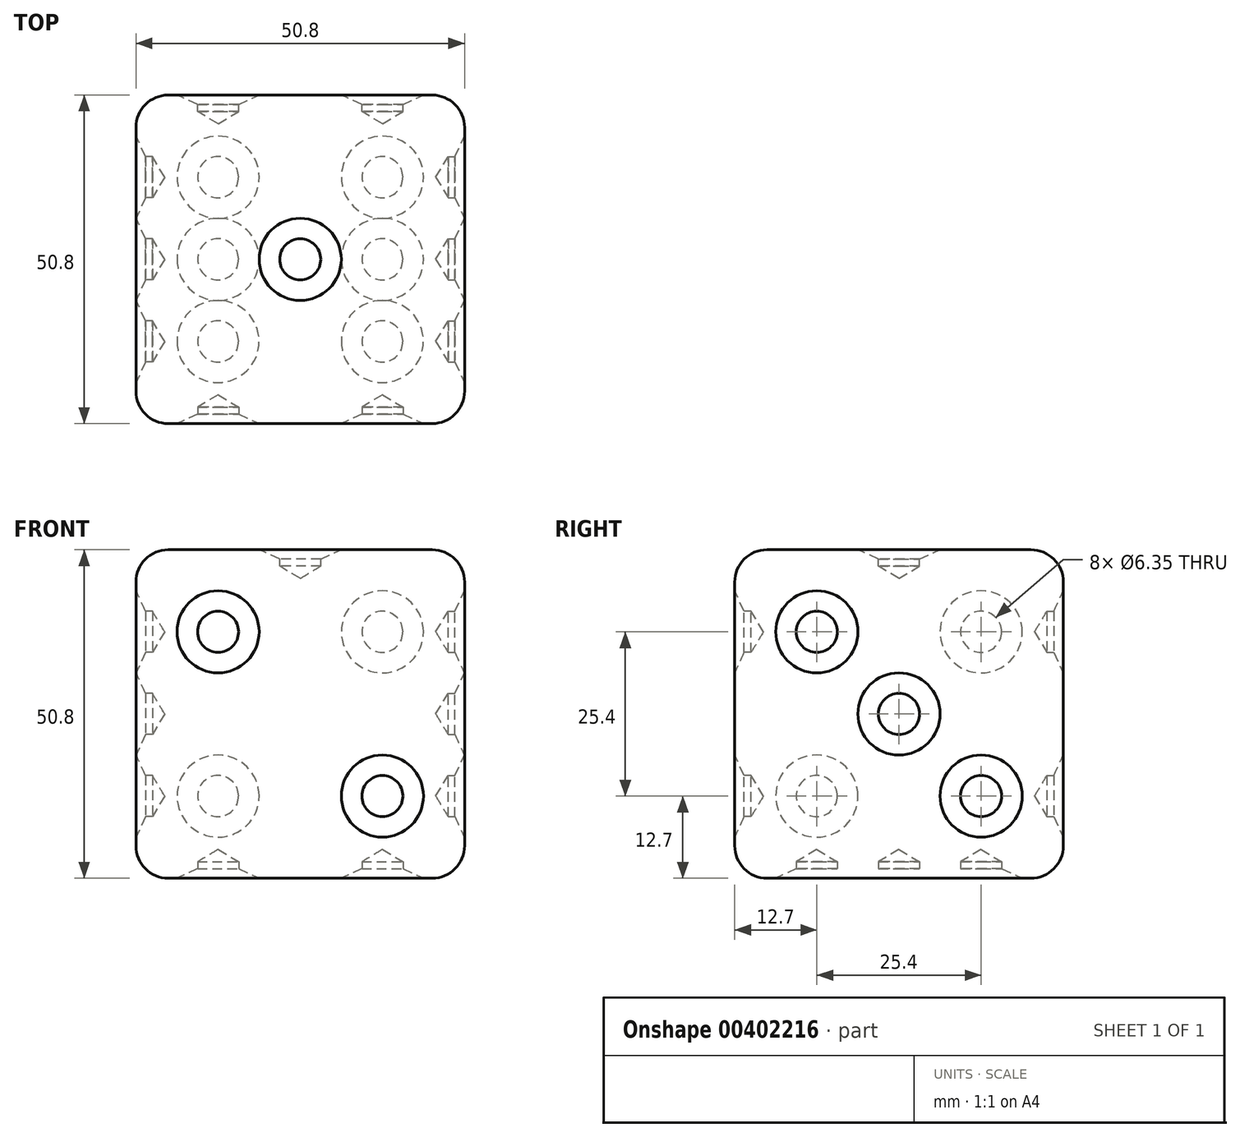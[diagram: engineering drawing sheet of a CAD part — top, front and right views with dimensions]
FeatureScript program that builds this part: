
annotation { "Feature Type Name" : "Feature", "Feature Type Description" : "" }
export const myFeature = defineFeature(function(context is Context, id is Id, definition is map)
    precondition{}
    {
        {
            var Q0;
            Q0=qCreatedBy(makeId("Top.planeOp"),FACE);
            var sketch = newSketch(context, id + "F0", { "sketchPlane" : qUnion([Q0])});
            skLineSegment(sketch, "E0.bottom", {"start": v(25.4, 25.4) * mm, "end": v(-25.4, 25.4) * mm});
            skLineSegment(sketch, "E0.top", {"start": v(25.4, -25.4) * mm, "end": v(-25.4, -25.4) * mm});
            skLineSegment(sketch, "E0.left", {"start": v(25.4, 25.4) * mm, "end": v(25.4, -25.4) * mm});
            skLineSegment(sketch, "E0.right", {"start": v(-25.4, 25.4) * mm, "end": v(-25.4, -25.4) * mm});
            skPoint(sketch, "E0.middle", {"position": v(0, 0) * mm});
            skSolve(sketch);
        }
        {
            var Q0;
            Q0=qSketchRegion(id+"F0",true);
            extrude(context, id + "F1", {"entities" : qUnion([Q0]), "depth" : 50.8 * mm});
        }
        {
            var Q0;
            Q0=makeQuery(id+"F1.opExtrude","CAP_FACE",FACE,{"disambiguationData":[OSD([sQuery(id+"F0.wireOp",EDGE,"E0.bottom"),sQuery(id+"F0.wireOp",EDGE,"E0.top"),sQuery(id+"F0.wireOp",EDGE,"E0.left"),sQuery(id+"F0.wireOp",EDGE,"E0.right")])],"isStart":false});
            var sketch = newSketch(context, id + "F2", { "sketchPlane" : qUnion([Q0])});
            skCircle(sketch, "E1", {"center": v(0, 0) * mm, "radius": 4.13 * mm});
            skSolve(sketch);
        }
        {
            var Q0;
            Q0=sQuery(id+"F2.wireOp",VERTEX,"E1.center");
            var Q1;
            Q1=makeQuery(id+"F1.opExtrude","SWEPT_BODY",BODY,{"disambiguationData":[OSD([sQuery(id+"F0.wireOp",EDGE,"E0.bottom"),sQuery(id+"F0.wireOp",EDGE,"E0.top"),sQuery(id+"F0.wireOp",EDGE,"E0.left"),sQuery(id+"F0.wireOp",EDGE,"E0.right")])]});
            hole(context, id + "F3", {"style" : HoleStyle.C_SINK, "endStyle" : HoleEndStyle.BLIND, "holeDiameter" : 6.35 * mm, "cSinkDiameter" : 12.7 * mm, "cSinkAngle" : 130 * degree, "holeDepth" : 2.54 * mm, "isTappedThrough" : true, "tappedDepth" : 12.7 * mm, "tapClearance" : 3, "locations" : qUnion([Q0]), "scope" : qUnion([Q1])});
        }
        {
            var Q0;
            Q0=makeQuery(id+"F1.opExtrude","SWEPT_FACE",FACE,{"disambiguationData":[OSD([sQuery(id+"F0.wireOp",EDGE,"E0.top")])]});
            var sketch = newSketch(context, id + "F4", { "sketchPlane" : qUnion([Q0])});
            skLineSegment(sketch, "E2", {"start": v(-25.4, 50.8) * mm, "end": v(-25.4, 38.1) * mm});
            skLineSegment(sketch, "E3", {"start": v(-12.7, 38.1) * mm, "end": v(-25.4, 38.1) * mm});
            skLineSegment(sketch, "E4", {"start": v(-12.7, 38.1) * mm, "end": v(-12.7, 50.8) * mm});
            skLineSegment(sketch, "E5", {"start": v(-25.4, 50.8) * mm, "end": v(-12.7, 50.8) * mm});
            skLineSegment(sketch, "E6", {"start": v(25.4, 0) * mm, "end": v(12.7, 0) * mm});
            skLineSegment(sketch, "E7", {"start": v(12.7, 0) * mm, "end": v(12.7, 12.7) * mm});
            skLineSegment(sketch, "E8", {"start": v(12.7, 12.7) * mm, "end": v(25.4, 12.7) * mm});
            skLineSegment(sketch, "E9", {"start": v(25.4, 12.7) * mm, "end": v(25.4, 0) * mm});
            skSolve(sketch);
        }
        {
            var Q0;
            Q0=sQuery(id+"F4.wireOp",VERTEX,"E4.start");
            var Q1;
            Q1=sQuery(id+"F4.wireOp",VERTEX,"E8.start");
            var Q2;
            Q2=makeQuery(id+"F1.opExtrude","SWEPT_BODY",BODY,{"disambiguationData":[OSD([sQuery(id+"F0.wireOp",EDGE,"E0.bottom"),sQuery(id+"F0.wireOp",EDGE,"E0.top"),sQuery(id+"F0.wireOp",EDGE,"E0.left"),sQuery(id+"F0.wireOp",EDGE,"E0.right")])]});
            hole(context, id + "F5", {"style" : HoleStyle.C_SINK, "endStyle" : HoleEndStyle.BLIND, "holeDiameter" : 6.35 * mm, "cSinkDiameter" : 12.7 * mm, "cSinkAngle" : 130 * degree, "holeDepth" : 2.54 * mm, "isTappedThrough" : true, "tappedDepth" : 12.7 * mm, "tapClearance" : 3, "locations" : qUnion([Q0, Q1]), "scope" : qUnion([Q2])});
        }
        {
            var Q0;
            Q0=makeQuery(id+"F1.opExtrude","SWEPT_FACE",FACE,{"disambiguationData":[OSD([sQuery(id+"F0.wireOp",EDGE,"E0.left")])]});
            var sketch = newSketch(context, id + "F6", { "sketchPlane" : qUnion([Q0])});
            skLineSegment(sketch, "E10", {"start": v(0, 50.8) * mm, "end": v(0, 0) * mm, "construction": true});
            skLineSegment(sketch, "E11", {"start": v(0, 0) * mm, "end": v(0, 25.4) * mm, "construction": true});
            skLineSegment(sketch, "E12", {"start": v(25.4, 25.4) * mm, "end": v(0, 25.4) * mm, "construction": true});
            skLineSegment(sketch, "E13", {"start": v(0, 25.4) * mm, "end": v(-25.4, 25.4) * mm, "construction": true});
            skCircle(sketch, "E14", {"center": v(0, 25.4) * mm, "radius": 2.62 * mm});
            skLineSegment(sketch, "E15", {"start": v(-12.7, 50.8) * mm, "end": v(-12.7, 38.1) * mm});
            skLineSegment(sketch, "E16", {"start": v(-25.4, 38.1) * mm, "end": v(-25.4, 50.8) * mm});
            skLineSegment(sketch, "E17", {"start": v(-12.7, 50.8) * mm, "end": v(-25.4, 50.8) * mm});
            skLineSegment(sketch, "E18", {"start": v(-12.7, 38.1) * mm, "end": v(-25.4, 38.1) * mm});
            skLineSegment(sketch, "E19", {"start": v(25.4, 50.8) * mm, "end": v(-25.4, 0) * mm, "construction": true});
            skLineSegment(sketch, "E20.MirrorCS", {"start": v(25.4, 12.7) * mm, "end": v(12.7, 12.7) * mm});
            skLineSegment(sketch, "E21.MirrorCS", {"start": v(12.7, 12.7) * mm, "end": v(12.7, 0) * mm});
            skCircle(sketch, "E22", {"center": v(-12.7, 38.1) * mm, "radius": 8.2 * mm});
            skCircle(sketch, "E23", {"center": v(12.7, 12.7) * mm, "radius": 11.3 * mm});
            skSolve(sketch);
        }
        {
            var Q0;
            Q0=sQuery(id+"F6.wireOp",VERTEX,"E18.start");
            var Q1;
            Q1=sQuery(id+"F6.wireOp",VERTEX,"E12.end");
            var Q2;
            Q2=sQuery(id+"F6.wireOp",VERTEX,"E21.MirrorCS.start");
            var Q3;
            Q3=makeQuery(id+"F1.opExtrude","SWEPT_BODY",BODY,{"disambiguationData":[OSD([sQuery(id+"F0.wireOp",EDGE,"E0.bottom"),sQuery(id+"F0.wireOp",EDGE,"E0.top"),sQuery(id+"F0.wireOp",EDGE,"E0.left"),sQuery(id+"F0.wireOp",EDGE,"E0.right")])]});
            hole(context, id + "F7", {"style" : HoleStyle.C_SINK, "endStyle" : HoleEndStyle.BLIND, "holeDiameter" : 6.35 * mm, "cSinkDiameter" : 12.7 * mm, "cSinkAngle" : 130 * degree, "holeDepth" : 2.54 * mm, "isTappedThrough" : true, "tappedDepth" : 12.7 * mm, "tapClearance" : 3, "locations" : qUnion([Q0, Q1, Q2]), "scope" : qUnion([Q3])});
        }
        {
            var Q0;
            Q0=makeQuery(id+"F1.opExtrude","SWEPT_FACE",FACE,{"disambiguationData":[OSD([sQuery(id+"F0.wireOp",EDGE,"E0.bottom")])]});
            var sketch = newSketch(context, id + "F8", { "sketchPlane" : qUnion([Q0])});
            skLineSegment(sketch, "E24", {"start": v(12.7, 50.8) * mm, "end": v(12.7, 38.1) * mm, "construction": true});
            skLineSegment(sketch, "E25", {"start": v(12.7, 38.1) * mm, "end": v(25.4, 38.1) * mm, "construction": true});
            skLineSegment(sketch, "E26", {"start": v(-25.4, 50.8) * mm, "end": v(25.4, 0) * mm});
            skLineSegment(sketch, "E27", {"start": v(25.4, 50.8) * mm, "end": v(-25.4, 0) * mm});
            skLineSegment(sketch, "E28", {"start": v(0, 50.8) * mm, "end": v(0, 0) * mm});
            skLineSegment(sketch, "E29.MirrorCS", {"start": v(-12.7, 50.8) * mm, "end": v(-12.7, 38.1) * mm, "construction": true});
            skLineSegment(sketch, "E30.MirrorCS", {"start": v(-12.7, 38.1) * mm, "end": v(-25.4, 38.1) * mm, "construction": true});
            skLineSegment(sketch, "E31.MirrorCS", {"start": v(-25.4, 12.7) * mm, "end": v(-12.7, 12.7) * mm, "construction": true});
            skLineSegment(sketch, "E32.MirrorCS", {"start": v(-12.7, 12.7) * mm, "end": v(-12.7, 0) * mm, "construction": true});
            skLineSegment(sketch, "E33.MirrorCS", {"start": v(25.4, 12.7) * mm, "end": v(12.7, 12.7) * mm, "construction": true});
            skLineSegment(sketch, "E34.MirrorCS", {"start": v(12.7, 12.7) * mm, "end": v(12.7, 0) * mm, "construction": true});
            skSolve(sketch);
        }
        {
            var Q0;
            Q0=sQuery(id+"F8.wireOp",VERTEX,"E30.MirrorCS.start");
            var Q1;
            Q1=sQuery(id+"F8.wireOp",VERTEX,"E24.end");
            var Q2;
            Q2=sQuery(id+"F8.wireOp",VERTEX,"E33.MirrorCS.end");
            var Q3;
            Q3=sQuery(id+"F8.wireOp",VERTEX,"E31.MirrorCS.end");
            var Q4;
            Q4=makeQuery(id+"F1.opExtrude","SWEPT_BODY",BODY,{"disambiguationData":[OSD([sQuery(id+"F0.wireOp",EDGE,"E0.bottom"),sQuery(id+"F0.wireOp",EDGE,"E0.top"),sQuery(id+"F0.wireOp",EDGE,"E0.left"),sQuery(id+"F0.wireOp",EDGE,"E0.right")])]});
            hole(context, id + "F9", {"style" : HoleStyle.C_SINK, "endStyle" : HoleEndStyle.BLIND, "holeDiameter" : 6.35 * mm, "cSinkDiameter" : 12.7 * mm, "cSinkAngle" : 130 * degree, "holeDepth" : 2.54 * mm, "isTappedThrough" : true, "tappedDepth" : 12.7 * mm, "tapClearance" : 3, "locations" : qUnion([Q0, Q1, Q2, Q3]), "scope" : qUnion([Q4])});
        }
        {
            var Q0;
            Q0=makeQuery(id+"F1.opExtrude","SWEPT_FACE",FACE,{"disambiguationData":[OSD([sQuery(id+"F0.wireOp",EDGE,"E0.right")])]});
            var sketch = newSketch(context, id + "F10", { "sketchPlane" : qUnion([Q0])});
            skLineSegment(sketch, "E35", {"start": v(0, 50.8) * mm, "end": v(0, 0) * mm, "construction": true});
            skLineSegment(sketch, "E36", {"start": v(-25.4, 25.4) * mm, "end": v(25.4, 25.4) * mm, "construction": true});
            skLineSegment(sketch, "E37", {"start": v(25.4, 25.4) * mm, "end": v(25.4, 38.1) * mm, "construction": true});
            skLineSegment(sketch, "E38", {"start": v(25.4, 38.1) * mm, "end": v(12.7, 38.1) * mm, "construction": true});
            skLineSegment(sketch, "E39", {"start": v(12.7, 38.1) * mm, "end": v(12.7, 50.8) * mm, "construction": true});
            skLineSegment(sketch, "E40", {"start": v(25.4, 50.8) * mm, "end": v(-25.4, 0) * mm, "construction": true});
            skLineSegment(sketch, "E41", {"start": v(-25.4, 0) * mm, "end": v(-25.4, 50.8) * mm, "construction": true});
            skLineSegment(sketch, "E42", {"start": v(-25.4, 50.8) * mm, "end": v(25.4, 0) * mm, "construction": true});
            skLineSegment(sketch, "E43.MirrorCS", {"start": v(-12.7, 38.1) * mm, "end": v(-12.7, 50.8) * mm, "construction": true});
            skLineSegment(sketch, "E44.MirrorCS", {"start": v(-25.4, 38.1) * mm, "end": v(-12.7, 38.1) * mm, "construction": true});
            skLineSegment(sketch, "E45.MirrorCS", {"start": v(12.7, 12.7) * mm, "end": v(25.4, 12.7) * mm, "construction": true});
            skLineSegment(sketch, "E46.MirrorCS", {"start": v(12.7, 0) * mm, "end": v(12.7, 12.7) * mm, "construction": true});
            skLineSegment(sketch, "E47.MirrorCS", {"start": v(-12.7, 12.7) * mm, "end": v(-25.4, 12.7) * mm, "construction": true});
            skLineSegment(sketch, "E48.MirrorCS", {"start": v(-12.7, 0) * mm, "end": v(-12.7, 12.7) * mm, "construction": true});
            skCircle(sketch, "E49", {"center": v(0, 25.4) * mm, "radius": 3.7 * mm});
            skSolve(sketch);
        }
        {
            var Q0;
            Q0=sQuery(id+"F10.wireOp",VERTEX,"E44.MirrorCS.end");
            var Q1;
            Q1=sQuery(id+"F10.wireOp",VERTEX,"E38.end");
            var Q2;
            Q2=sQuery(id+"F10.wireOp",VERTEX,"E45.MirrorCS.start");
            var Q3;
            Q3=sQuery(id+"F10.wireOp",VERTEX,"E47.MirrorCS.start");
            var Q4;
            Q4=sQuery(id+"F6.wireOp",VERTEX,"E12.end");
            var Q5;
            Q5=sQuery(id+"F10.wireOp",VERTEX,"E49.center");
            var Q6;
            Q6=makeQuery(id+"F1.opExtrude","SWEPT_BODY",BODY,{"disambiguationData":[OSD([sQuery(id+"F0.wireOp",EDGE,"E0.bottom"),sQuery(id+"F0.wireOp",EDGE,"E0.top"),sQuery(id+"F0.wireOp",EDGE,"E0.left"),sQuery(id+"F0.wireOp",EDGE,"E0.right")])]});
            hole(context, id + "F11", {"style" : HoleStyle.C_SINK, "endStyle" : HoleEndStyle.BLIND, "holeDiameter" : 6.35 * mm, "cSinkDiameter" : 12.7 * mm, "cSinkAngle" : 130 * degree, "holeDepth" : 2.54 * mm, "isTappedThrough" : true, "tappedDepth" : 12.7 * mm, "tapClearance" : 3, "locations" : qUnion([Q0, Q1, Q2, Q3, Q4, Q5]), "scope" : qUnion([Q6])});
        }
        {
            var Q0;
            Q0=makeQuery(id+"F1.opExtrude","CAP_FACE",FACE,{"disambiguationData":[OSD([sQuery(id+"F0.wireOp",EDGE,"E0.bottom"),sQuery(id+"F0.wireOp",EDGE,"E0.top"),sQuery(id+"F0.wireOp",EDGE,"E0.left"),sQuery(id+"F0.wireOp",EDGE,"E0.right")])],"isStart":true});
            var sketch = newSketch(context, id + "F12", { "sketchPlane" : qUnion([Q0])});
            skLineSegment(sketch, "E50", {"start": v(-12.7, 12.7) * mm, "end": v(-25.4, 12.7) * mm, "construction": true});
            skLineSegment(sketch, "E51", {"start": v(-25.4, 12.7) * mm, "end": v(-25.4, 0.99) * mm, "construction": true});
            skLineSegment(sketch, "E52", {"start": v(-12.7, -12.7) * mm, "end": v(-25.4, -12.7) * mm, "construction": true});
            skLineSegment(sketch, "E53", {"start": v(-12.7, 12.7) * mm, "end": v(-12.7, 25.4) * mm, "construction": true});
            skLineSegment(sketch, "E54", {"start": v(-12.7, -12.7) * mm, "end": v(-12.7, -25.4) * mm, "construction": true});
            skLineSegment(sketch, "E55", {"start": v(-12.7, 12.7) * mm, "end": v(-12.7, -12.7) * mm});
            skLineSegment(sketch, "E56", {"start": v(-12.7, 0) * mm, "end": v(-25.4, 0) * mm});
            skCircle(sketch, "E57", {"center": v(-19.05, 0) * mm, "radius": 3.76 * mm});
            skLineSegment(sketch, "E58", {"start": v(0, 25.4) * mm, "end": v(0, -25.4) * mm, "construction": true});
            skLineSegment(sketch, "E59.MirrorCS", {"start": v(12.7, 12.7) * mm, "end": v(12.7, 25.4) * mm, "construction": true});
            skLineSegment(sketch, "E60.MirrorCS", {"start": v(12.7, 12.7) * mm, "end": v(25.4, 12.7) * mm, "construction": true});
            skCircle(sketch, "E61.MirrorC", {"center": v(19.05, 0) * mm, "radius": 3.76 * mm});
            skLineSegment(sketch, "E62.MirrorCS", {"start": v(12.7, -12.7) * mm, "end": v(25.4, -12.7) * mm, "construction": true});
            skLineSegment(sketch, "E63.MirrorCS", {"start": v(12.7, -12.7) * mm, "end": v(12.7, -25.4) * mm, "construction": true});
            skLineSegment(sketch, "E64.MirrorCS", {"start": v(12.7, 12.7) * mm, "end": v(12.7, -12.7) * mm});
            skLineSegment(sketch, "E65.MirrorCS", {"start": v(12.7, 0) * mm, "end": v(25.4, 0) * mm});
            skSolve(sketch);
        }
        {
            var Q0;
            Q0=sQuery(id+"F12.wireOp",VERTEX,"E53.start");
            var Q1;
            Q1=sQuery(id+"F12.wireOp",VERTEX,"E56.start");
            var Q2;
            Q2=sQuery(id+"F12.wireOp",VERTEX,"E54.start");
            var Q3;
            Q3=sQuery(id+"F12.wireOp",VERTEX,"E64.MirrorCS.start");
            var Q4;
            Q4=sQuery(id+"F12.wireOp",VERTEX,"E65.MirrorCS.start");
            var Q5;
            Q5=sQuery(id+"F12.wireOp",VERTEX,"E64.MirrorCS.end");
            var Q6;
            Q6=makeQuery(id+"F1.opExtrude","SWEPT_BODY",BODY,{"disambiguationData":[OSD([sQuery(id+"F0.wireOp",EDGE,"E0.bottom"),sQuery(id+"F0.wireOp",EDGE,"E0.top"),sQuery(id+"F0.wireOp",EDGE,"E0.left"),sQuery(id+"F0.wireOp",EDGE,"E0.right")])]});
            hole(context, id + "F13", {"style" : HoleStyle.C_SINK, "endStyle" : HoleEndStyle.BLIND, "holeDiameter" : 6.35 * mm, "cSinkDiameter" : 12.7 * mm, "cSinkAngle" : 130 * degree, "holeDepth" : 2.54 * mm, "isTappedThrough" : true, "tappedDepth" : 12.7 * mm, "tapClearance" : 3, "locations" : qUnion([Q0, Q1, Q2, Q3, Q4, Q5]), "scope" : qUnion([Q6])});
        }
        {
            var Q0;
            Q0=makeQuery(id+"F1.opExtrude","CAP_EDGE",EDGE,{"disambiguationData":[OSD([sQuery(id+"F0.wireOp",EDGE,"E0.top")])],"isStart":false});
            var Q1;
            Q1=makeQuery(id+"F1.opExtrude","CAP_EDGE",EDGE,{"disambiguationData":[OSD([sQuery(id+"F0.wireOp",EDGE,"E0.left")])],"isStart":false});
            var Q2;
            Q2=makeQuery(id+"F1.opExtrude","SWEPT_EDGE",EDGE,{"disambiguationData":[OSD([sQuery(id+"F0.wireOp",EDGE,"E0.top"),sQuery(id+"F0.wireOp",EDGE,"E0.left")])]});
            var Q3;
            Q3=makeQuery(id+"F1.opExtrude","CAP_EDGE",EDGE,{"disambiguationData":[OSD([sQuery(id+"F0.wireOp",EDGE,"E0.right")])],"isStart":false});
            var Q4;
            Q4=makeQuery(id+"F1.opExtrude","CAP_EDGE",EDGE,{"disambiguationData":[OSD([sQuery(id+"F0.wireOp",EDGE,"E0.bottom")])],"isStart":false});
            var Q5;
            Q5=makeQuery(id+"F1.opExtrude","SWEPT_EDGE",EDGE,{"disambiguationData":[OSD([sQuery(id+"F0.wireOp",EDGE,"E0.top"),sQuery(id+"F0.wireOp",EDGE,"E0.right")])]});
            var Q6;
            Q6=makeQuery(id+"F1.opExtrude","CAP_EDGE",EDGE,{"disambiguationData":[OSD([sQuery(id+"F0.wireOp",EDGE,"E0.top")])],"isStart":true});
            var Q7;
            Q7=makeQuery(id+"F1.opExtrude","CAP_EDGE",EDGE,{"disambiguationData":[OSD([sQuery(id+"F0.wireOp",EDGE,"E0.left")])],"isStart":true});
            var Q8;
            Q8=makeQuery(id+"F1.opExtrude","CAP_EDGE",EDGE,{"disambiguationData":[OSD([sQuery(id+"F0.wireOp",EDGE,"E0.right")])],"isStart":true});
            var Q9;
            Q9=makeQuery(id+"F1.opExtrude","CAP_EDGE",EDGE,{"disambiguationData":[OSD([sQuery(id+"F0.wireOp",EDGE,"E0.bottom")])],"isStart":true});
            var Q10;
            Q10=makeQuery(id+"F1.opExtrude","SWEPT_EDGE",EDGE,{"disambiguationData":[OSD([sQuery(id+"F0.wireOp",EDGE,"E0.bottom"),sQuery(id+"F0.wireOp",EDGE,"E0.left")])]});
            var Q11;
            Q11=makeQuery(id+"F1.opExtrude","SWEPT_EDGE",EDGE,{"disambiguationData":[OSD([sQuery(id+"F0.wireOp",EDGE,"E0.bottom"),sQuery(id+"F0.wireOp",EDGE,"E0.right")])]});
            fillet(context, id + "F14", {"entities" : qUnion([Q0, Q1, Q2, Q3, Q4, Q5, Q6, Q7, Q8, Q9, Q10, Q11]), "radius" : 5 * mm, "tangentPropagation" : true, "allowEdgeOverflow" : false});
        }
    });
